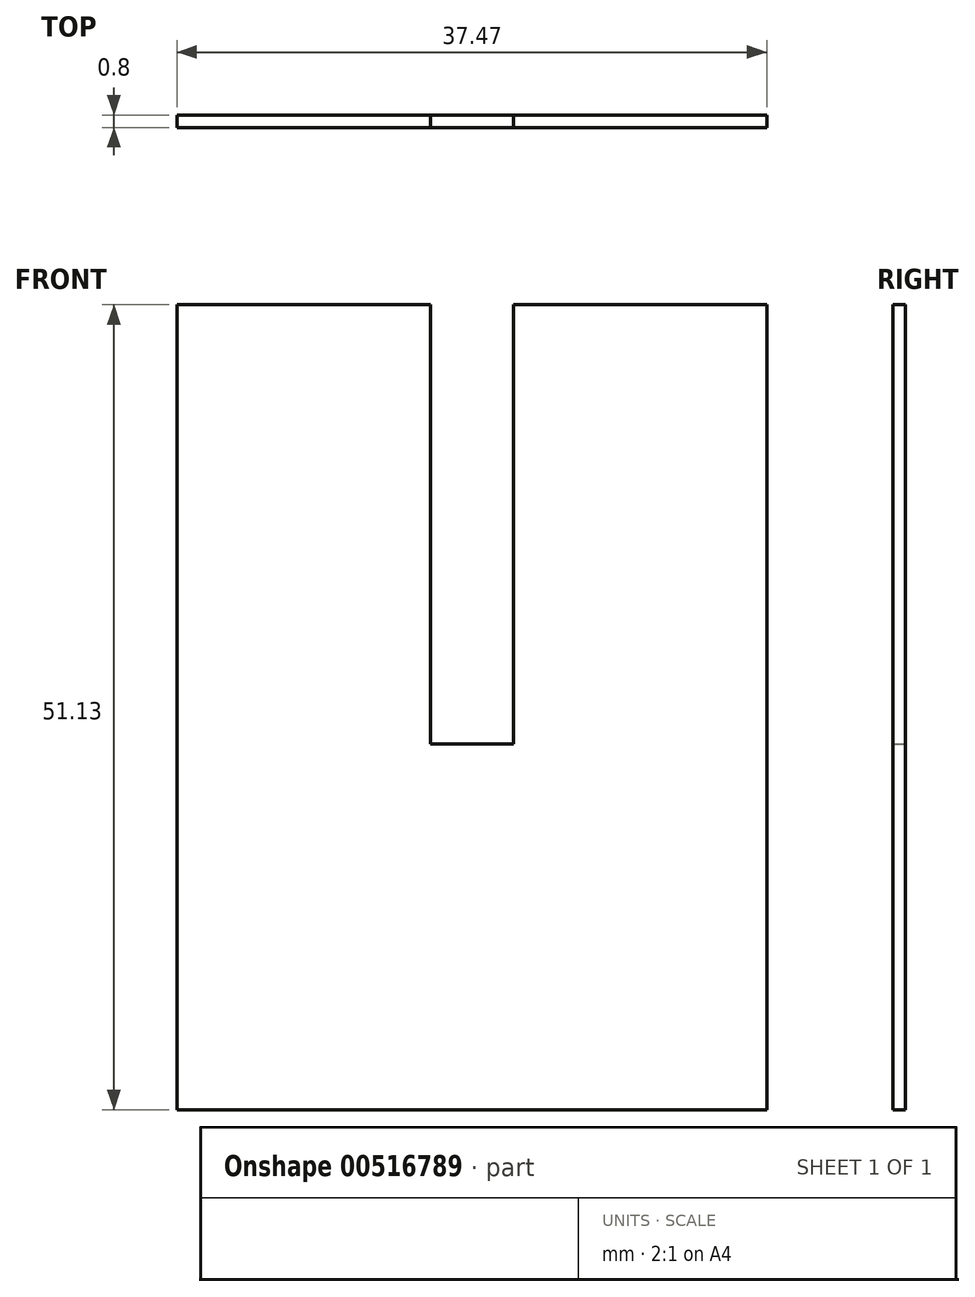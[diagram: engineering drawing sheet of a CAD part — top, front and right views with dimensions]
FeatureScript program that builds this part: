
annotation { "Feature Type Name" : "Feature", "Feature Type Description" : "" }
export const myFeature = defineFeature(function(context is Context, id is Id, definition is map)
    precondition{}
    {
        {
            var Q0;
            Q0=qCreatedBy(makeId("Front.planeOp"),FACE);
            var sketch = newSketch(context, id + "F0", { "sketchPlane" : qUnion([Q0])});
            skLineSegment(sketch, "E0.bottom", {"start": v(0, 0) * mm, "end": v(37.47, 0) * mm});
            skLineSegment(sketch, "E0.left", {"start": v(0, 0) * mm, "end": v(0, 51.13) * mm});
            skLineSegment(sketch, "E0.right", {"start": v(37.47, 0) * mm, "end": v(37.47, 51.13) * mm});
            skLineSegment(sketch, "E1.trimOffspring", {"start": v(21.37, 51.13) * mm, "end": v(37.47, 51.13) * mm});
            skLineSegment(sketch, "E2", {"start": v(16.1, 51.13) * mm, "end": v(0, 51.13) * mm});
            skLineSegment(sketch, "E3", {"start": v(16.1, 51.13) * mm, "end": v(16.1, 23.23) * mm});
            skLineSegment(sketch, "E4", {"start": v(15.85, 23.23) * mm, "end": v(21.37, 23.23) * mm});
            skLineSegment(sketch, "E5", {"start": v(21.37, 23.23) * mm, "end": v(21.37, 51.13) * mm});
            skSolve(sketch);
        }
        {
            var Q0;
            Q0 = qSketchRegion(id + "F0", true);
            extrude(context, id + "F1", {"entities" : qUnion([Q0]), "depth" : 0.8 * mm, "offsetDistance" : 25.4 * mm});
        }
    });
